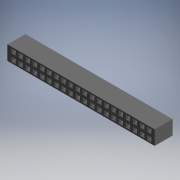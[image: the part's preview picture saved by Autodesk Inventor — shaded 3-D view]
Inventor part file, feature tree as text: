
AUTODESK INVENTOR PART (.ipt)
format: ipt  version: 2017.3 (Build 213256000, 256)  size: 764,928 bytes
history: native  units: mm (DEFAULTED — no unit token found)
features: other x63, extrude x4, sketch x4, pattern_linear x2
ambient origin geometry x8: Origin, YZ Plane, XZ Plane, XY Plane, X Axis, Y Axis, Z Axis, Center Point
bodies: Solid1 (feature_tree)
feature tree (73):
  extrude  "Extrusion1"  Depth=0.889mm TaperAngle=0.0deg
  extrude  "Extrusion2"  Depth=2.54mm TaperAngle=0.0deg
  extrude  "Extrusion3"  Depth=2.54mm TaperAngle=0.0deg
  pattern_linear  "Rectangular Pattern1"  [2 undecoded]
  extrude  "Extrusion4"  [1 undecoded]
  pattern_linear  "Rectangular Pattern2"  [2 undecoded]
  other  "lower_body_to_cable_XY"
  other  "lower_body_to_cable_YZ"
  other  "lower_body_to_cable_ZX"
  other  "lower_body_to_cable_X"
  other  "lower_body_to_cable_Y"
  other  "lower_body_to_cable_Z"
  other  "lower_body_to_cable_Center"
  other  "lower_body_to_dummy_XY"
  other  "lower_body_to_dummy_YZ"
  other  "lower_body_to_dummy_ZX"
  other  "lower_body_to_dummy_X"
  other  "lower_body_to_dummy_Y"
  other  "lower_body_to_dummy_Z"
  other  "lower_body_to_dummy_Center"
  other  "lower_body_to_dummy_reverse_XY"
  other  "lower_body_to_dummy_reverse_YZ"
  other  "lower_body_to_dummy_reverse_ZX"
  other  "lower_body_to_dummy_reverse_X"
  other  "lower_body_to_dummy_reverse_Y"
  other  "lower_body_to_dummy_reverse_Z"
  other  "lower_body_to_dummy_reverse_Center"
  other  "lower_body_to_upper_body_XY"
  other  "lower_body_to_upper_body_YZ"
  other  "lower_body_to_upper_body_ZX"
  other  "lower_body_to_upper_body_X"
  other  "lower_body_to_upper_body_Y"
  other  "lower_body_to_upper_body_Z"
  other  "lower_body_to_upper_body_Center"
  other  "lower_body_to_upper_body_reverse_XY"
  other  "lower_body_to_upper_body_reverse_YZ"
  other  "lower_body_to_upper_body_reverse_ZX"
  other  "lower_body_to_upper_body_reverse_X"
  other  "lower_body_to_upper_body_reverse_Y"
  other  "lower_body_to_upper_body_reverse_Z"
  other  "lower_body_to_upper_body_reverse_Center"
  other  "pin_XY"
  other  "pin_YZ"
  other  "pin_ZX"
  other  "pin_X"
  other  "pin_Y"
  other  "pin_Z"
  other  "pin_Center"
  other  "pin2_XY"
  other  "pin2_YZ"
  other  "pin2_ZX"
  other  "pin2_X"
  other  "pin2_Y"
  other  "pin2_Z"
  other  "pin2_Center"
  other  "pin2_reverse_XY"
  other  "pin2_reverse_YZ"
  other  "pin2_reverse_ZX"
  other  "pin2_reverse_X"
  other  "pin2_reverse_Y"
  other  "pin2_reverse_Z"
  other  "pin2_reverse_Center"
  other  "pin_reverse_XY"
  other  "pin_reverse_YZ"
  other  "pin_reverse_ZX"
  other  "pin_reverse_X"
  other  "pin_reverse_Y"
  other  "pin_reverse_Z"
  other  "pin_reverse_Center"
  sketch  "Sketch_1"  dims[d0=6.35mm d1=0.0mm d2=0.889mm d3=0.0mm]
  sketch  "Sketch_3"  dims[d4=0.4572mm d5=-6.94641mm d6=200.0mm d8=2.54mm d9=10.0mm d11=0.0mm]
  sketch  "Sketch_4"  dims[d12=0.4572mm d13=-6.94641mm d14=200.0mm d16=2.54mm d17=10.0mm d19=0.0mm]
  sketch  "Sketch_7"  dims[d20=0.0mm d21=0.0mm]
note: 5 required parameter values undecoded (feature->parameter linkage not recoverable at this tier; creation-order binding heuristic only, values carry confidence <= 0.55)
